# Revit family: GLAM_230x150x6.5
name_source: partatom
category: Plumbing Fixtures
revit_build: Autodesk Revit 2018 (Build: 20170223_1515(x64)
units: mm (PartAtom-declared; Revit-internal decimal feet)

## family parameters
Always vertical = Yes
Cut with Voids When Loaded = No
OmniClass Number = 23.45.00.00
OmniClass Title = Sanitary, Laundry, and Cleaning Equipment
Part Type = Normal
Room Calculation Point = No
Round Connector Dimension = Use Diameter
Shared = No
Work Plane-Based = Yes

## types (3) — shared parameters
BIM object developer = www.concepsysbim.com
CONTROL_Actuation type = Mécanique
CONTROL_Brief description = Plaque de commande mécanique en abs
CONTROL_Height = 150 mm
CONTROL_Length = 230 mm  [stored 0.754593 ft]
CONTROL_Material = ABS
CONTROL_Model = Glam
CONTROL_Product data url = https://www.regiplast.fr
CONTROL_Type of flush = Double-Débit
CONTROL_Type/function = Plaque de Commande pour réservoir à encastrer
CONTROL_Width = 6.5 mm
Default Elevation = 1219.2 mm  [stored 4 ft]
Description = Plaque de commande mécanique en abs
Model = Glam
Product data url = https://www.regiplast.fr
URL = https://www.regiplast.fr

## per-type parameters (varying)
| type | CONTROL_Model Series | CONTROL_Model code/ref |
| Mécanique_Blanche | Blanche | 184B |
| Mécanique_Chromée | Chromée | 184C |
| Mécanique_Chromée Mate | Chromée Mate | 184M |

note: [stored X ft] marks values corroborated as IEEE doubles in the binary element streams (Revit-internal decimal feet)

## geometry (parser evidence)
native form markers: Sweep x4
no freeform markers — native parametric forms only
